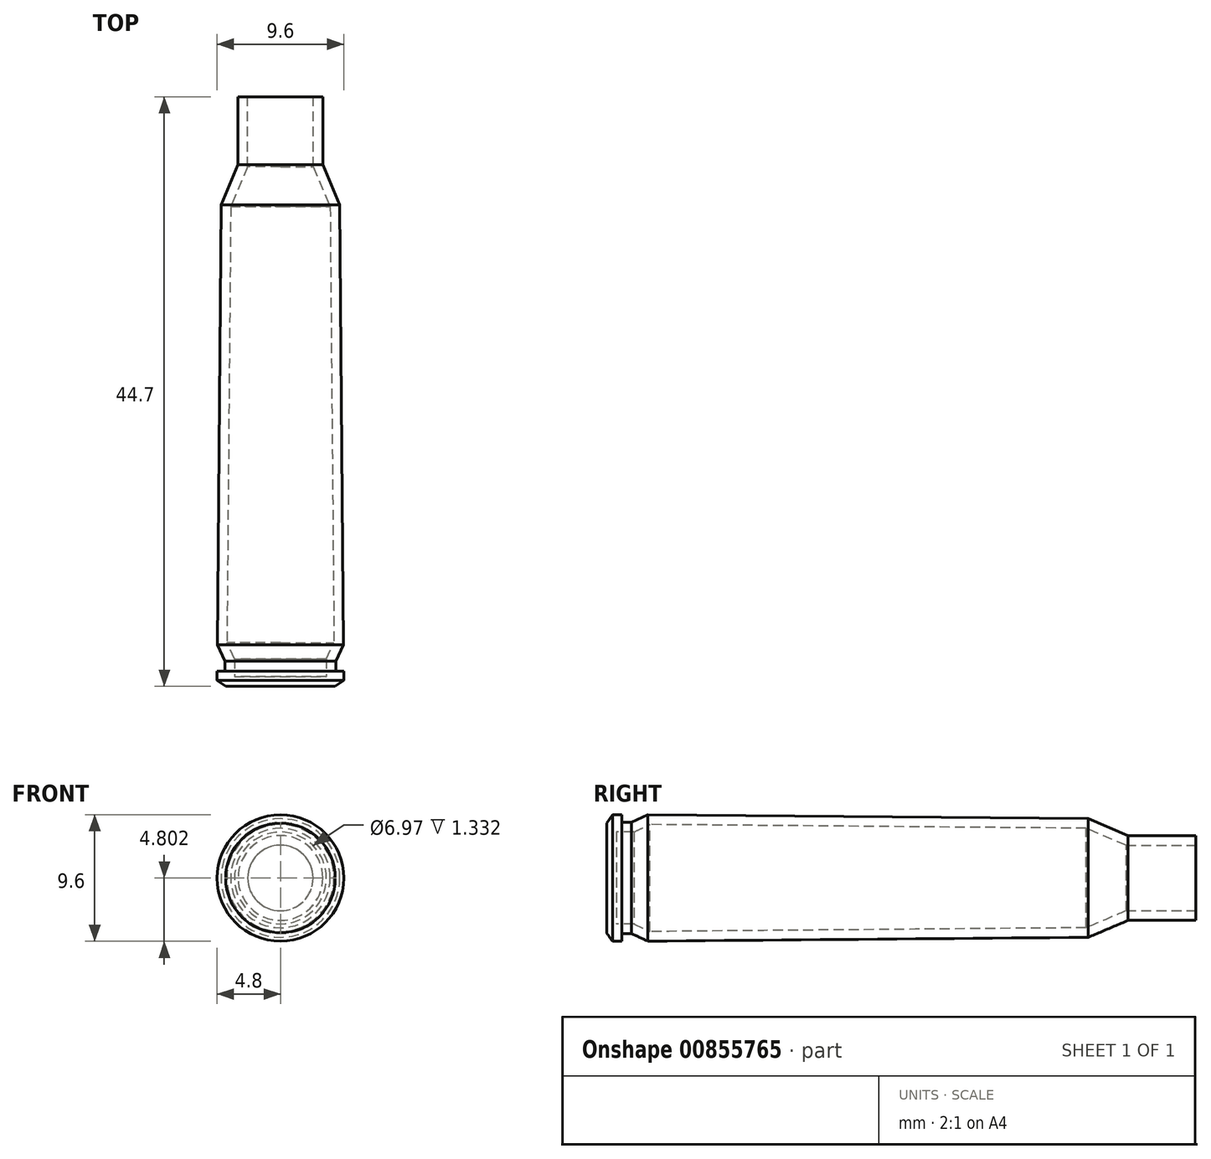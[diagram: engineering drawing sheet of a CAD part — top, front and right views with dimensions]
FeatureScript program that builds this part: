
annotation { "Feature Type Name" : "Feature", "Feature Type Description" : "" }
export const myFeature = defineFeature(function(context is Context, id is Id, definition is map)
    precondition{}
    {
        {
            var Q0;
            Q0=qCreatedBy(makeId("Right.planeOp"),FACE);
            var sketch = newSketch(context, id + "F0", { "sketchPlane" : qUnion([Q0])});
            skPoint(sketch, "E0", {"position": v(82.2, 16.38) * mm});
            skPoint(sketch, "E1", {"position": v(82.2, 21.18) * mm});
            skLineSegment(sketch, "E2", {"start": v(82.2, 21.18) * mm, "end": v(81.5, 21.18) * mm});
            skLineSegment(sketch, "E3", {"start": v(82.2, 16.38) * mm, "end": v(80.5, 16.38) * mm, "construction": true});
            skLineSegment(sketch, "E4", {"start": v(81.05, 21.18) * mm, "end": v(81.05, 16.38) * mm});
            skPoint(sketch, "E5", {"position": v(81.5, 21.18) * mm});
            skLineSegment(sketch, "E6", {"start": v(81.5, 21.18) * mm, "end": v(81.05, 20.54) * mm});
            skPoint(sketch, "E7", {"position": v(84.18, 16.38) * mm});
            skPoint(sketch, "E8", {"position": v(84.18, 21.17) * mm});
            skLineSegment(sketch, "E9", {"start": v(84.18, 21.17) * mm, "end": v(82.95, 20.6) * mm});
            skPoint(sketch, "E10", {"position": v(117.57, 16.38) * mm});
            skPoint(sketch, "E11", {"position": v(117.57, 20.88) * mm});
            skLineSegment(sketch, "E12", {"start": v(84.18, 21.17) * mm, "end": v(117.57, 20.88) * mm});
            skPoint(sketch, "E13", {"position": v(82.95, 16.38) * mm});
            skLineSegment(sketch, "E14", {"start": v(82.2, 21.18) * mm, "end": v(82.2, 20.6) * mm});
            skLineSegment(sketch, "E15", {"start": v(82.95, 20.6) * mm, "end": v(82.2, 20.6) * mm});
            skPoint(sketch, "E16", {"position": v(120.6, 16.38) * mm});
            skLineSegment(sketch, "E17", {"start": v(117.57, 20.88) * mm, "end": v(120.6, 19.6) * mm});
            skPoint(sketch, "E18", {"position": v(81.05, 16.38) * mm});
            skPoint(sketch, "E19", {"position": v(125.75, 16.38) * mm});
            skPoint(sketch, "E20", {"position": v(125.75, 19.6) * mm});
            skLineSegment(sketch, "E21", {"start": v(120.6, 19.6) * mm, "end": v(125.75, 19.6) * mm});
            skLineSegment(sketch, "E22", {"start": v(125.75, 19.6) * mm, "end": v(125.75, 16.38) * mm});
            skLineSegment(sketch, "E23", {"start": v(81.05, 16.38) * mm, "end": v(125.75, 16.38) * mm});
            skSolve(sketch);
        }
        {
            var Q0;
            Q0=makeQuery(id+"F0.imprint","IMPRINT",FACE,{"disambiguationData":[TD([[makeQuery(id+"F0.imprint","IMPRINT",EDGE,{"derivedFrom":sQuery(id+"F0.wireOp",EDGE,"E2")}),1.0]])]});
            var Q1;
            Q1=sQuery(id+"F0.wireOp",EDGE,"E23");
            revolve(context, id + "F1", {"surfaceOperationType" : NewSurfaceOperationType.NEW, "entities" : qUnion([Q0]), "axis" : qUnion([Q1]), "revolveType" : RevolveType.FULL});
        }
        {
            var Q0;
            Q0=makeQuery(id+"F1.opRevolve","SWEPT_FACE",FACE,{"disambiguationData":[OSD([sQuery(id+"F0.wireOp",EDGE,"E22")])]});
            shell(context, id + "F2", {"entities" : qUnion([Q0]), "thickness" : 6.43 * mm - 5.7 * mm});
        }
    });
